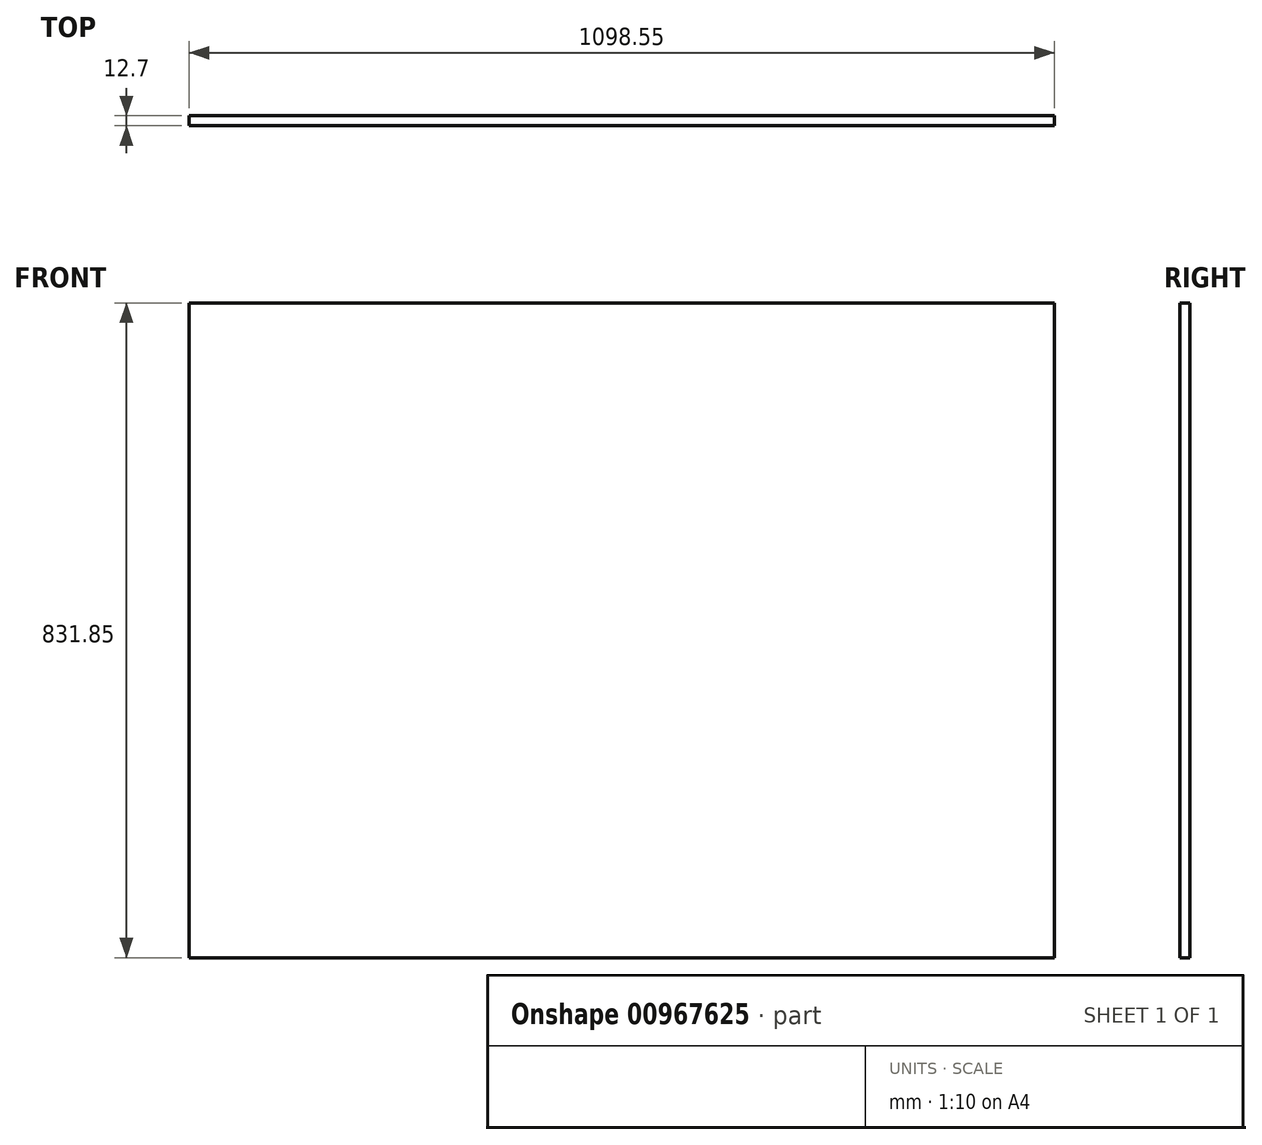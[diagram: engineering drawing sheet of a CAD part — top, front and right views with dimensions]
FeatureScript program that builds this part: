
annotation { "Feature Type Name" : "Feature", "Feature Type Description" : "" }
export const myFeature = defineFeature(function(context is Context, id is Id, definition is map)
    precondition{}
    {
        {
            var Q0;
            Q0=qCreatedBy(makeId("Front.planeOp"),FACE);
            var sketch = newSketch(context, id + "F0", { "sketchPlane" : qUnion([Q0])});
            skLineSegment(sketch, "E0.bottom", {"start": v(0, 0) * mm, "end": v(1098.55, 0) * mm});
            skLineSegment(sketch, "E0.top", {"start": v(0, 831.85) * mm, "end": v(1098.55, 831.85) * mm});
            skLineSegment(sketch, "E0.left", {"start": v(0, 0) * mm, "end": v(0, 831.85) * mm});
            skLineSegment(sketch, "E0.right", {"start": v(1098.55, 0) * mm, "end": v(1098.55, 831.85) * mm});
            skSolve(sketch);
        }
        {
            var Q0;
            Q0 = qSketchRegion(id + "F0", true);
            extrude(context, id + "F1", {"entities" : qUnion([Q0]), "depth" : 12.7 * mm, "offsetDistance" : 25.4 * mm});
        }
    });
